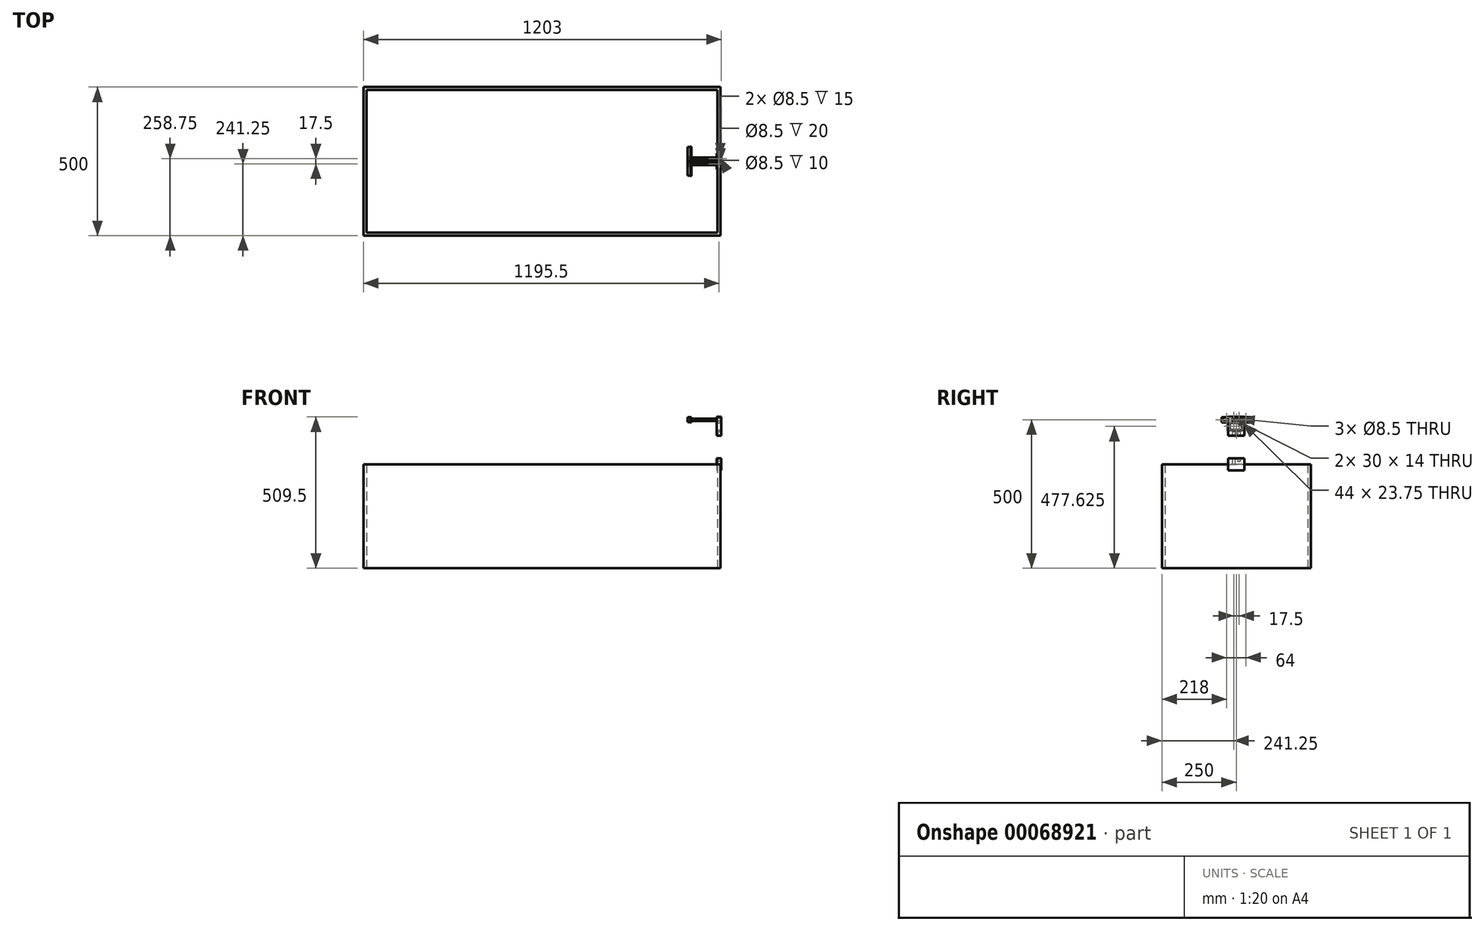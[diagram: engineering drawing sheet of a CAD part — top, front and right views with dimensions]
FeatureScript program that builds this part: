
annotation { "Feature Type Name" : "Feature", "Feature Type Description" : "" }
export const myFeature = defineFeature(function(context is Context, id is Id, definition is map)
    precondition{}
    {
        {
            var Q0;
            Q0=qCreatedBy(makeId("Right.planeOp"),FACE);
            var sketch = newSketch(context, id + "F0", { "sketchPlane" : qUnion([Q0])});
            skLineSegment(sketch, "E0.rect.bottom", {"start": v(-49.5, 9) * mm, "end": v(49.5, 9) * mm});
            skLineSegment(sketch, "E0.rect.top", {"start": v(-49.5, -9) * mm, "end": v(49.5, -9) * mm});
            skLineSegment(sketch, "E0.rect.left", {"start": v(-49.5, 9) * mm, "end": v(-49.5, -9) * mm});
            skLineSegment(sketch, "E0.rect.right", {"start": v(49.5, 9) * mm, "end": v(49.5, -9) * mm});
            skLineSegment(sketch, "E1.bottom", {"start": v(-49.5, -9) * mm, "end": v(0, -9) * mm, "construction": true});
            skLineSegment(sketch, "E1.top", {"start": v(-49.5, 9) * mm, "end": v(0, 9) * mm, "construction": true});
            skLineSegment(sketch, "E2", {"start": v(0, 9) * mm, "end": v(0, -9) * mm, "construction": true});
            skPoint(sketch, "E3.middle", {"position": v(0, 0) * mm});
            skLineSegment(sketch, "E4.bottom", {"start": v(-48, 8) * mm, "end": v(-16, 8) * mm});
            skLineSegment(sketch, "E4.top", {"start": v(-48, -8) * mm, "end": v(-16, -8) * mm});
            skLineSegment(sketch, "E4.left", {"start": v(-48, 8) * mm, "end": v(-48, -8) * mm});
            skLineSegment(sketch, "E5.MirrorCS", {"start": v(48, 8) * mm, "end": v(48, -8) * mm});
            skLineSegment(sketch, "E6.MirrorCS", {"start": v(48, 8) * mm, "end": v(16, 8) * mm});
            skLineSegment(sketch, "E7.MirrorCS", {"start": v(48, -8) * mm, "end": v(16, -8) * mm});
            skLineSegment(sketch, "E8.bottom", {"start": v(50, 9.5) * mm, "end": v(-50, 9.5) * mm});
            skLineSegment(sketch, "E8.top", {"start": v(50, -9.5) * mm, "end": v(-50, -9.5) * mm});
            skLineSegment(sketch, "E8.left", {"start": v(50, 9.5) * mm, "end": v(50, -9.5) * mm});
            skLineSegment(sketch, "E8.right", {"start": v(-50, 9.5) * mm, "end": v(-50, -9.5) * mm});
            skCircle(sketch, "E9", {"center": v(-8.75, 0) * mm, "radius": 4.25 * mm});
            skCircle(sketch, "E10.MirrorC", {"center": v(8.75, 0) * mm, "radius": 4.25 * mm});
            skLineSegment(sketch, "E11.bottom", {"start": v(0.75, 9.5) * mm, "end": v(-0.75, 9.5) * mm});
            skLineSegment(sketch, "E11.top", {"start": v(0.75, -9.5) * mm, "end": v(-0.75, -9.5) * mm});
            skLineSegment(sketch, "E11.left", {"start": v(0.75, 9.5) * mm, "end": v(0.75, -9.5) * mm});
            skLineSegment(sketch, "E11.right", {"start": v(-0.75, 9.5) * mm, "end": v(-0.75, -9.5) * mm});
            skLineSegment(sketch, "E12.0", {"start": v(47, 7) * mm, "end": v(17, 7) * mm});
            skLineSegment(sketch, "E12.1", {"start": v(47, 7) * mm, "end": v(47, -7) * mm});
            skLineSegment(sketch, "E12.2", {"start": v(47, -7) * mm, "end": v(17, -7) * mm});
            skLineSegment(sketch, "E12.3", {"start": v(17, 7) * mm, "end": v(17, -7) * mm});
            skLineSegment(sketch, "E13.MirrorCS", {"start": v(-47, 7) * mm, "end": v(-17, 7) * mm});
            skLineSegment(sketch, "E14.MirrorCS", {"start": v(-17, 7) * mm, "end": v(-17, -7) * mm});
            skLineSegment(sketch, "E15.MirrorCS", {"start": v(-47, -7) * mm, "end": v(-17, -7) * mm});
            skLineSegment(sketch, "E16.MirrorCS", {"start": v(-47, 7) * mm, "end": v(-47, -7) * mm});
            skLineSegment(sketch, "E17.bottom", {"start": v(-13, -8) * mm, "end": v(13, -8) * mm});
            skLineSegment(sketch, "E17.top", {"start": v(-13, 8) * mm, "end": v(13, 8) * mm});
            skLineSegment(sketch, "E18", {"start": v(-16, -8) * mm, "end": v(-13, -8) * mm});
            skLineSegment(sketch, "E19", {"start": v(-16, 8) * mm, "end": v(-13, 8) * mm});
            skLineSegment(sketch, "E20", {"start": v(13, -8) * mm, "end": v(16, -8) * mm});
            skLineSegment(sketch, "E21", {"start": v(13, 8) * mm, "end": v(16, 8) * mm});
            skPoint(sketch, "E3.left.end.orphan", {"position": v(-13, -6) * mm});
            skPoint(sketch, "E22.trimOffspring.start.orphan", {"position": v(-13, 6) * mm});
            skPoint(sketch, "E3.right.end.orphan", {"position": v(13, -6) * mm});
            skPoint(sketch, "E3.right.start.orphan", {"position": v(13, 6) * mm});
            skSolve(sketch);
        }
        {
            var Q0;
            Q0=makeQuery(id+"F0.imprint","IMPRINT",FACE,{"disambiguationData":[TD([[makeQuery(id+"F0.imprint","IMPRINT",EDGE,{"derivedFrom":sQuery(id+"F0.wireOp",EDGE,"E0.rect.bottom")}),-1.0]])]});
            var Q1;
            Q1=makeQuery(id+"F0.imprint","IMPRINT",FACE,{"disambiguationData":[TD([[makeQuery(id+"F0.imprint","IMPRINT",EDGE,{"derivedFrom":sQuery(id+"F0.wireOp",EDGE,"E3.bottom")}),-1.0]])]});
            var Q2;
            {var subQ0=sQuery(id+"F0.wireOp",EDGE,"E11.right");var subQ1=sQuery(id+"F0.wireOp",EDGE,"E0.rect.top");var subQ2=makeQuery(id+"F0.imprint","INTERSECT",VERTEX,{"derivedFrom":[subQ1,subQ0]});Q2=makeQuery(id+"F0.imprint","IMPRINT",FACE,{"disambiguationData":[TD([[makeQuery(id+"F0.imprint","IMPRINT",EDGE,{"disambiguationData":[TD([[subQ2,-1.0]])],"derivedFrom":subQ1}),1.0]])]});}
            var Q3;
            {var subQ4=sQuery(id+"F0.wireOp",EDGE,"E0.rect.right");Q3=makeQuery(id+"F0.imprint","IMPRINT",FACE,{"disambiguationData":[TD([[makeQuery(id+"F0.imprint","IMPRINT",EDGE,{"derivedFrom":subQ4}),-1.0]])]});}
            var Q4;
            {var subQ0=sQuery(id+"F0.wireOp",EDGE,"E3.right");Q4=makeQuery(id+"F0.imprint","IMPRINT",FACE,{"disambiguationData":[TD([[makeQuery(id+"F0.imprint","IMPRINT",EDGE,{"derivedFrom":subQ0}),-1.0]])]});}
            var Q5;
            {var subQ5=sQuery(id+"F0.wireOp",EDGE,"E3.left");Q5=makeQuery(id+"F0.imprint","IMPRINT",FACE,{"disambiguationData":[TD([[makeQuery(id+"F0.imprint","IMPRINT",EDGE,{"derivedFrom":subQ5}),1.0]])]});}
            var Q6;
            {var subQ0=sQuery(id+"F0.wireOp",EDGE,"E0.rect.left");Q6=makeQuery(id+"F0.imprint","IMPRINT",FACE,{"disambiguationData":[TD([[makeQuery(id+"F0.imprint","IMPRINT",EDGE,{"derivedFrom":subQ0}),1.0]])]});}
            var Q7;
            {var subQ0=sQuery(id+"F0.wireOp",EDGE,"E17.top");var subQ1=sQuery(id+"F0.wireOp",EDGE,"E11.left");var subQ2=makeQuery(id+"F0.imprint","INTERSECT",VERTEX,{"derivedFrom":[subQ1,subQ0]});Q7=makeQuery(id+"F0.imprint","IMPRINT",FACE,{"disambiguationData":[TD([[makeQuery(id+"F0.imprint","IMPRINT",EDGE,{"disambiguationData":[TD([[subQ2,-1.0]])],"derivedFrom":subQ1}),-1.0]])]});}
            var Q8;
            Q8=makeQuery(id+"F0.imprint","IMPRINT",FACE,{"disambiguationData":[TD([[makeQuery(id+"F0.imprint","IMPRINT",EDGE,{"derivedFrom":sQuery(id+"F0.wireOp",EDGE,"E10.MirrorC")}),1.0]])]});
            extrude(context, id + "F1", {"entities" : qUnion([Q0, Q1, Q2, Q3, Q4, Q5, Q6, Q7, Q8]), "depth" : 2 * mm});
        }
        {
            var Q0;
            Q0=makeQuery(id+"F0.imprint","IMPRINT",FACE,{"disambiguationData":[TD([[makeQuery(id+"F0.imprint","IMPRINT",EDGE,{"derivedFrom":sQuery(id+"F0.wireOp",EDGE,"E4.bottom")}),-1.0]])]});
            var Q1;
            Q1=makeQuery(id+"F0.imprint","IMPRINT",FACE,{"disambiguationData":[TD([[makeQuery(id+"F0.imprint","IMPRINT",EDGE,{"derivedFrom":sQuery(id+"F0.wireOp",EDGE,"E5.MirrorCS")}),-1.0]])]});
            var Q2;
            {var subQ0=sQuery(id+"F0.wireOp",EDGE,"E3.right");Q2=makeQuery(id+"F0.imprint","IMPRINT",FACE,{"disambiguationData":[TD([[makeQuery(id+"F0.imprint","IMPRINT",EDGE,{"derivedFrom":subQ0}),-1.0]])]});}
            var Q3;
            {var subQ5=sQuery(id+"F0.wireOp",EDGE,"E3.left");Q3=makeQuery(id+"F0.imprint","IMPRINT",FACE,{"disambiguationData":[TD([[makeQuery(id+"F0.imprint","IMPRINT",EDGE,{"derivedFrom":subQ5}),1.0]])]});}
            var Q4;
            Q4=makeQuery(id+"F0.imprint","IMPRINT",FACE,{"disambiguationData":[TD([[makeQuery(id+"F0.imprint","IMPRINT",EDGE,{"derivedFrom":sQuery(id+"F0.wireOp",EDGE,"E10.MirrorC")}),1.0]])]});
            extrude(context, id + "F2", {"entities" : qUnion([Q0, Q1, Q2, Q3, Q4]), "operationType" : NewBodyOperationType.ADD, "oppositeDirection" : true, "depth" : 10 * mm, "hasSecondDirection" : true, "secondDirectionOppositeDirection" : false, "secondDirectionDepth" : 2 * mm});
        }
        {
            var Q0;
            Q0=qSketchRegion(id+"F0",true);
            var Q1;
            Q1=sQuery(id+"F0.wireOp",EDGE,"E8.right");
            var Q2;
            Q2=sQuery(id+"F0.wireOp",EDGE,"E8.top");
            var Q3;
            Q3=sQuery(id+"F0.wireOp",EDGE,"E8.left");
            var Q4;
            Q4=sQuery(id+"F0.wireOp",EDGE,"E8.bottom");
            extrude(context, id + "F3", {"entities" : qUnion([Q0]), "bodyType" : ToolBodyType.SURFACE, "surfaceEntities" : qUnion([Q1, Q2, Q3, Q4]), "oppositeDirection" : true, "depth" : 1000 * mm});
        }
        {
            var Q0;
            Q0=qCreatedBy(makeId("Top.planeOp"),FACE);
            cPlane(context, id + "F4", {"entities" : qUnion([Q0]), "cplaneType" : CPlaneType.OFFSET, "offset" : 500 * mm, "oppositeDirection" : true, "width" : 150 * mm, "height" : 150 * mm});
        }
        {
            var Q0;
            Q0=qCreatedBy(id+"F4.planeOp",FACE);
            var sketch = newSketch(context, id + "F5", { "sketchPlane" : qUnion([Q0])});
            skLineSegment(sketch, "E23.0", {"start": v(-1100, 250) * mm, "end": v(100, 250) * mm});
            skLineSegment(sketch, "E24.0", {"start": v(-1090, 240) * mm, "end": v(-1090, -240) * mm});
            skLineSegment(sketch, "E25.0", {"start": v(-1100, 250) * mm, "end": v(-1100, -250) * mm});
            skLineSegment(sketch, "E26.0", {"start": v(-1100, -250) * mm, "end": v(100, -250) * mm});
            skLineSegment(sketch, "E27.0", {"start": v(-1090, -240) * mm, "end": v(90, -240) * mm});
            skLineSegment(sketch, "E28.0", {"start": v(100, 250) * mm, "end": v(100, -250) * mm});
            skLineSegment(sketch, "E29.0", {"start": v(90, 240) * mm, "end": v(90, -240) * mm});
            skLineSegment(sketch, "E30.0", {"start": v(-1090, 240) * mm, "end": v(90, 240) * mm});
            skSolve(sketch);
        }
        {
            var Q0;
            Q0=qSketchRegion(id+"F5",true);
            extrude(context, id + "F6", {"entities" : qUnion([Q0]), "depth" : 350 * mm});
        }
        {
            var Q0;
            Q0=makeQuery(id+"F6.opExtrude","SWEPT_FACE",FACE,{"disambiguationData":[OSD([sQuery(id+"F5.wireOp",EDGE,"E28.0")])]});
            var sketch = newSketch(context, id + "F7", { "sketchPlane" : qUnion([Q0])});
            skLineSegment(sketch, "E31", {"start": v(0, 0) * mm, "end": v(0, -150) * mm, "construction": true});
            skLineSegment(sketch, "E32", {"start": v(0, -150) * mm, "end": v(0, -500) * mm, "construction": true});
            skLineSegment(sketch, "E33.0", {"start": v(-49.5, -9) * mm, "end": v(49.5, -9) * mm});
            skSolve(sketch);
        }
        {
            var Q0;
            Q0=makeQuery(id+"F6.opExtrude","CAP_FACE",FACE,{"disambiguationData":[OSD([sQuery(id+"F5.wireOp",EDGE,"E23.0"),sQuery(id+"F5.wireOp",EDGE,"E24.0"),sQuery(id+"F5.wireOp",EDGE,"E25.0"),sQuery(id+"F5.wireOp",EDGE,"E26.0"),sQuery(id+"F5.wireOp",EDGE,"E27.0"),sQuery(id+"F5.wireOp",EDGE,"E28.0"),sQuery(id+"F5.wireOp",EDGE,"E29.0"),sQuery(id+"F5.wireOp",EDGE,"E30.0")])],"isStart":false});
            var sketch = newSketch(context, id + "F8", { "sketchPlane" : qUnion([Q0])});
            skLineSegment(sketch, "E34", {"start": v(0, 25) * mm, "end": v(90, 25) * mm, "construction": true});
            skLineSegment(sketch, "E35", {"start": v(0, -25) * mm, "end": v(90, -25) * mm, "construction": true});
            skLineSegment(sketch, "E36.bottom", {"start": v(90, 25) * mm, "end": v(101, 25) * mm});
            skLineSegment(sketch, "E36.top", {"start": v(90, -25) * mm, "end": v(101, -25) * mm});
            skLineSegment(sketch, "E36.left", {"start": v(90, 25) * mm, "end": v(90, -25) * mm});
            skLineSegment(sketch, "E36.right", {"start": v(101, 25) * mm, "end": v(101, -25) * mm});
            skLineSegment(sketch, "E37.0", {"start": v(88, 27) * mm, "end": v(103, 27) * mm});
            skLineSegment(sketch, "E37.1", {"start": v(88, 27) * mm, "end": v(88, -27) * mm});
            skLineSegment(sketch, "E37.2", {"start": v(88, -27) * mm, "end": v(103, -27) * mm});
            skLineSegment(sketch, "E37.3", {"start": v(103, 27) * mm, "end": v(103, -27) * mm});
            skLineSegment(sketch, "E38", {"start": v(90, 25) * mm, "end": v(90, 27) * mm});
            skLineSegment(sketch, "E39", {"start": v(101, 25) * mm, "end": v(101, 27) * mm});
            skLineSegment(sketch, "E40", {"start": v(90, -25) * mm, "end": v(90, -27) * mm});
            skLineSegment(sketch, "E41", {"start": v(101, -25) * mm, "end": v(101, -27) * mm});
            skLineSegment(sketch, "E42", {"start": v(0, 0) * mm, "end": v(105.96, 0) * mm, "construction": true});
            skLineSegment(sketch, "E43", {"start": v(103, 0) * mm, "end": v(88, 0) * mm, "construction": true});
            skLineSegment(sketch, "E44.0", {"start": v(2, 4.5) * mm, "end": v(2, 13) * mm, "construction": true});
            skLineSegment(sketch, "E45", {"start": v(2, 13) * mm, "end": v(108.62, 13) * mm, "construction": true});
            skLineSegment(sketch, "E46", {"start": v(2, 4.5) * mm, "end": v(108.62, 4.5) * mm, "construction": true});
            skLineSegment(sketch, "E47", {"start": v(95.5, -27) * mm, "end": v(95.5, 0) * mm, "construction": true});
            skPoint(sketch, "E47.endSnap0", {"position": v(95.5, 27) * mm});
            skLineSegment(sketch, "E48.trimOffspring", {"start": v(95.5, 25) * mm, "end": v(95.5, 32.34) * mm, "construction": true});
            skLineSegment(sketch, "E49.trimOffspring", {"start": v(95.5, 4.5) * mm, "end": v(95.5, 13) * mm, "construction": true});
            skCircle(sketch, "E50", {"center": v(95.5, 8.75) * mm, "radius": 4.25 * mm});
            skCircle(sketch, "E51.MirrorC", {"center": v(95.5, -8.75) * mm, "radius": 4.25 * mm});
            skSolve(sketch);
        }
        {
            var Q0;
            Q0=makeQuery(id+"F8.imprint","IMPRINT",FACE,{"disambiguationData":[TD([[makeQuery(id+"F8.imprint","IMPRINT",EDGE,{"derivedFrom":sQuery(id+"F8.wireOp",EDGE,"E36.right")}),1.0]])]});
            var Q1;
            Q1=makeQuery(id+"F8.imprint","IMPRINT",FACE,{"disambiguationData":[TD([[makeQuery(id+"F8.imprint","IMPRINT",EDGE,{"derivedFrom":sQuery(id+"F8.wireOp",EDGE,"E36.left")}),-1.0]])]});
            var Q2;
            {var subQ0=sQuery(id+"F8.wireOp",EDGE,"E38");Q2=makeQuery(id+"F8.imprint","IMPRINT",FACE,{"disambiguationData":[TD([[makeQuery(id+"F8.imprint","IMPRINT",EDGE,{"derivedFrom":subQ0}),1.0]])]});}
            var Q3;
            {var subQ0=sQuery(id+"F8.wireOp",EDGE,"E39");Q3=makeQuery(id+"F8.imprint","IMPRINT",FACE,{"disambiguationData":[TD([[makeQuery(id+"F8.imprint","IMPRINT",EDGE,{"derivedFrom":subQ0}),1.0]])]});}
            var Q4;
            {var subQ0=sQuery(id+"F8.wireOp",EDGE,"E41");Q4=makeQuery(id+"F8.imprint","IMPRINT",FACE,{"disambiguationData":[TD([[makeQuery(id+"F8.imprint","IMPRINT",EDGE,{"derivedFrom":subQ0}),-1.0]])]});}
            var Q5;
            {var subQ0=sQuery(id+"F8.wireOp",EDGE,"E40");Q5=makeQuery(id+"F8.imprint","IMPRINT",FACE,{"disambiguationData":[TD([[makeQuery(id+"F8.imprint","IMPRINT",EDGE,{"derivedFrom":subQ0}),1.0]])]});}
            var Q6;
            {var subQ0=sQuery(id+"F8.wireOp",EDGE,"E36.right");Q6=makeQuery(id+"F8.imprint","IMPRINT",FACE,{"disambiguationData":[TD([[makeQuery(id+"F8.imprint","IMPRINT",EDGE,{"derivedFrom":subQ0}),-1.0]])]});}
            var Q7;
            {var subQ0=sQuery(id+"F8.wireOp",EDGE,"E36.left");Q7=makeQuery(id+"F8.imprint","IMPRINT",FACE,{"disambiguationData":[TD([[makeQuery(id+"F8.imprint","IMPRINT",EDGE,{"derivedFrom":subQ0}),1.0]])]});}
            var Q8;
            Q8=makeQuery(id+"F8.imprint","IMPRINT",FACE,{"disambiguationData":[TD([[makeQuery(id+"F8.imprint","IMPRINT",EDGE,{"derivedFrom":sQuery(id+"F8.wireOp",EDGE,"E50")}),1.0]])]});
            var Q9;
            Q9=makeQuery(id+"F8.imprint","IMPRINT",FACE,{"disambiguationData":[TD([[makeQuery(id+"F8.imprint","IMPRINT",EDGE,{"derivedFrom":sQuery(id+"F8.wireOp",EDGE,"E51.MirrorC")}),-1.0]])]});
            extrude(context, id + "F9", {"entities" : qUnion([Q0, Q1, Q2, Q3, Q4, Q5, Q6, Q7, Q8, Q9]), "depth" : 10 * mm});
        }
        {
            var Q0;
            Q0 = qSketchRegion(id + "F8", true);
            var Q1;
            {var subQ0=sQuery(id+"F8.wireOp",EDGE,"E36.left");Q1=makeQuery(id+"F8.imprint","IMPRINT",FACE,{"disambiguationData":[TD([[makeQuery(id+"F8.imprint","IMPRINT",EDGE,{"derivedFrom":subQ0}),1.0]])]});}
            var Q2;
            {var subQ0=sQuery(id+"F8.wireOp",EDGE,"E36.right");Q2=makeQuery(id+"F8.imprint","IMPRINT",FACE,{"disambiguationData":[TD([[makeQuery(id+"F8.imprint","IMPRINT",EDGE,{"derivedFrom":subQ0}),-1.0]])]});}
            extrude(context, id + "F10", {"entities" : qUnion([Q0, Q1, Q2]), "operationType" : NewBodyOperationType.ADD, "depth" : 20 * mm});
        }
        {
            var Q0;
            Q0=makeQuery(id+"F9.opExtrude","CAP_FACE",FACE,{"disambiguationData":[OSD([sQuery(id+"F8.wireOp",EDGE,"E37.0"),sQuery(id+"F8.wireOp",EDGE,"E37.1"),sQuery(id+"F8.wireOp",EDGE,"E37.2"),sQuery(id+"F8.wireOp",EDGE,"E37.3")])],"isStart":false});
            var sketch = newSketch(context, id + "F11", { "sketchPlane" : qUnion([Q0])});
            skCircle(sketch, "E52.0", {"center": v(95.5, 8.75) * mm, "radius": 4.25 * mm});
            skCircle(sketch, "E53.0", {"center": v(95.5, -8.75) * mm, "radius": 4.25 * mm});
            skSolve(sketch);
        }
        {
            var Q0;
            Q0=makeQuery(id+"F10.opExtrude","CAP_FACE",FACE,{"disambiguationData":[OSD([sQuery(id+"F8.wireOp",EDGE,"E37.0"),sQuery(id+"F8.wireOp",EDGE,"E37.1"),sQuery(id+"F8.wireOp",EDGE,"E37.2"),sQuery(id+"F8.wireOp",EDGE,"E37.3"),sQuery(id+"F8.wireOp",EDGE,"E50"),sQuery(id+"F8.wireOp",EDGE,"E51.MirrorC")])],"isStart":false});
            extrude(context, id + "F12", {"entities" : qUnion([Q0]), "operationType" : NewBodyOperationType.ADD, "oppositeDirection" : true, "depth" : 15 * mm});
        }
        {
            var Q0;
            Q0=makeQuery(id+"F8.imprint","IMPRINT",FACE,{"disambiguationData":[TD([[makeQuery(id+"F8.imprint","IMPRINT",EDGE,{"derivedFrom":sQuery(id+"F8.wireOp",EDGE,"E36.left")}),-1.0]])]});
            var Q1;
            Q1=makeQuery(id+"F8.imprint","IMPRINT",FACE,{"disambiguationData":[TD([[makeQuery(id+"F8.imprint","IMPRINT",EDGE,{"derivedFrom":sQuery(id+"F8.wireOp",EDGE,"E36.right")}),1.0]])]});
            extrude(context, id + "F13", {"entities" : qUnion([Q0, Q1]), "operationType" : NewBodyOperationType.ADD, "oppositeDirection" : true, "depth" : 20 * mm});
        }
        {
            var Q0;
            {var subQ0=sQuery(id+"F8.wireOp",EDGE,"E37.3");Q0=makeQuery(id+"F13.boolean.opBoolean","MERGE",FACE,{"derivedFrom":[makeQuery(id+"F9.opExtrude","SWEPT_FACE",FACE,{"disambiguationData":[OSD([subQ0])]}),makeQuery(id+"F13.opExtrude","SWEPT_FACE",FACE,{"disambiguationData":[OSD([subQ0])]})]});}
            var sketch = newSketch(context, id + "F14", { "sketchPlane" : qUnion([Q0])});
            skLineSegment(sketch, "E54.0", {"start": v(-27, -150) * mm, "end": v(-27, -170) * mm});
            skLineSegment(sketch, "E55.0", {"start": v(27, -150) * mm, "end": v(27, -170) * mm});
            skLineSegment(sketch, "E56.0", {"start": v(27, -150) * mm, "end": v(-27, -150) * mm});
            skCircle(sketch, "E57.0", {"center": v(-8.75, 0) * mm, "radius": 4.25 * mm});
            skCircle(sketch, "E58.0", {"center": v(8.75, 0) * mm, "radius": 4.25 * mm});
            skLineSegment(sketch, "E59.top", {"start": v(-27, 9.5) * mm, "end": v(27, 9.5) * mm});
            skLineSegment(sketch, "E59.left", {"start": v(-27, -54.25) * mm, "end": v(-27, 9.5) * mm});
            skLineSegment(sketch, "E59.right", {"start": v(27, -54.25) * mm, "end": v(27, 9.5) * mm});
            skLineSegment(sketch, "E60", {"start": v(-8.98, -10) * mm, "end": v(11.55, -10) * mm, "construction": true});
            skLineSegment(sketch, "E61.0", {"start": v(27, 9.5) * mm, "end": v(-27, 9.5) * mm});
            skLineSegment(sketch, "E62.0", {"start": v(-49.5, -9) * mm, "end": v(49.5, -9) * mm, "construction": true});
            skLineSegment(sketch, "E63.0", {"start": v(250, -150) * mm, "end": v(-250, -150) * mm, "construction": true});
            skLineSegment(sketch, "E64.0", {"start": v(27, -130) * mm, "end": v(-27, -130) * mm, "construction": true});
            skLineSegment(sketch, "E65", {"start": v(-27, -54.25) * mm, "end": v(27, -54.25) * mm});
            skLineSegment(sketch, "E66.bottom", {"start": v(-22, -34.25) * mm, "end": v(22, -34.25) * mm});
            skLineSegment(sketch, "E66.top", {"start": v(-22, -10.5) * mm, "end": v(22, -10.5) * mm});
            skLineSegment(sketch, "E66.left", {"start": v(-22, -34.25) * mm, "end": v(-22, -10.5) * mm});
            skLineSegment(sketch, "E66.right", {"start": v(22, -34.25) * mm, "end": v(22, -10.5) * mm});
            skPoint(sketch, "E67.MirrorC.center.orphan", {"position": v(-8.75, -40) * mm});
            skPoint(sketch, "E68.MirrorC.center.orphan", {"position": v(8.75, -40) * mm});
            skSolve(sketch);
        }
        {
            var Q0;
            Q0=qSketchRegion(id+"F14",true);
            var Q1;
            Q1=makeQuery(id+"F14.imprint","IMPRINT",FACE,{"disambiguationData":[TD([[makeQuery(id+"F14.imprint","IMPRINT",EDGE,{"derivedFrom":sQuery(id+"F14.wireOp",EDGE,"E57.0")}),-1.0]])]});
            extrude(context, id + "F15", {"entities" : qUnion([Q0, Q1]), "operationType" : NewBodyOperationType.ADD, "oppositeDirection" : true, "depth" : 15 * mm});
        }
        {
            var Q0;
            Q0=qCreatedBy(makeId("Top.planeOp"),FACE);
            var sketch = newSketch(context, id + "F16", { "sketchPlane" : qUnion([Q0])});
            skLineSegment(sketch, "E69.bottom", {"start": v(-7, -4.5) * mm, "end": v(103, -4.5) * mm});
            skLineSegment(sketch, "E69.top", {"start": v(-7, -8.5) * mm, "end": v(103, -8.5) * mm});
            skLineSegment(sketch, "E69.left", {"start": v(-7, -4.5) * mm, "end": v(-7, -8.5) * mm});
            skLineSegment(sketch, "E69.right", {"start": v(103, -4.5) * mm, "end": v(103, -8.5) * mm});
            skLineSegment(sketch, "E70", {"start": v(0, 0) * mm, "end": v(122.29, 0) * mm, "construction": true});
            skLineSegment(sketch, "E71.MirrorCS", {"start": v(-7, 4.5) * mm, "end": v(-7, 8.5) * mm});
            skLineSegment(sketch, "E72.MirrorCS", {"start": v(103, 4.5) * mm, "end": v(103, 8.5) * mm});
            skLineSegment(sketch, "E73.MirrorCS", {"start": v(-7, 8.5) * mm, "end": v(103, 8.5) * mm});
            skLineSegment(sketch, "E74.MirrorCS", {"start": v(-7, 4.5) * mm, "end": v(103, 4.5) * mm});
            skLineSegment(sketch, "E75.0", {"start": v(103, 4.5) * mm, "end": v(103, 13) * mm});
            skLineSegment(sketch, "E76.0", {"start": v(103, -4.5) * mm, "end": v(103, -13) * mm});
            skSolve(sketch);
        }
        {
            var Q0;
            Q0=makeQuery(id+"F16.imprint","IMPRINT",FACE,{"disambiguationData":[TD([[makeQuery(id+"F16.imprint","IMPRINT",EDGE,{"derivedFrom":sQuery(id+"F16.wireOp",EDGE,"E69.bottom")}),-1.0]])]});
            var Q1;
            Q1=sQuery(id+"F16.wireOp",EDGE,"E69.top");
            revolve(context, id + "F17", {"entities" : qUnion([Q0]), "axis" : qUnion([Q1]), "revolveType" : RevolveType.FULL});
        }
        {
            var Q0;
            Q0=makeQuery(id+"F16.imprint","IMPRINT",FACE,{"disambiguationData":[TD([[makeQuery(id+"F16.imprint","IMPRINT",EDGE,{"derivedFrom":sQuery(id+"F16.wireOp",EDGE,"E72.MirrorCS")}),1.0]])]});
            var Q1;
            {var subQ0=sQuery(id+"F16.wireOp",EDGE,"E71.MirrorCS");Q1=makeQuery(id+"F16.imprint","IMPRINT",FACE,{"disambiguationData":[TD([[makeQuery(id+"F16.imprint","IMPRINT",EDGE,{"derivedFrom":subQ0}),-1.0]])]});}
            var Q2;
            Q2=sQuery(id+"F16.wireOp",EDGE,"E73.MirrorCS");
            revolve(context, id + "F18", {"entities" : qUnion([Q0, Q1]), "axis" : qUnion([Q2]), "revolveType" : RevolveType.FULL});
        }
        {
            var Q0;
            Q0=makeQuery(id+"F15.opExtrude","SWEPT_FACE",FACE,{"disambiguationData":[OSD([sQuery(id+"F14.wireOp",EDGE,"E65")])]});
            var sketch = newSketch(context, id + "F19", { "sketchPlane" : qUnion([Q0])});
            skCircle(sketch, "E77.0", {"center": v(95.5, 8.75) * mm, "radius": 4.25 * mm});
            skCircle(sketch, "E78.0", {"center": v(95.5, -8.75) * mm, "radius": 4.25 * mm});
            skSolve(sketch);
        }
        {
            var Q0;
            Q0=makeQuery(id+"F19.imprint","IMPRINT",FACE,{"disambiguationData":[TD([[makeQuery(id+"F19.imprint","IMPRINT",EDGE,{"derivedFrom":sQuery(id+"F19.wireOp",EDGE,"E77.0")}),1.0]])]});
            var Q1;
            Q1=makeQuery(id+"F19.imprint","IMPRINT",FACE,{"disambiguationData":[TD([[makeQuery(id+"F19.imprint","IMPRINT",EDGE,{"derivedFrom":sQuery(id+"F19.wireOp",EDGE,"E78.0")}),1.0]])]});
            extrude(context, id + "F20", {"entities" : qUnion([Q0, Q1]), "operationType" : NewBodyOperationType.REMOVE, "oppositeDirection" : true, "depth" : 15 * mm});
        }
    });
